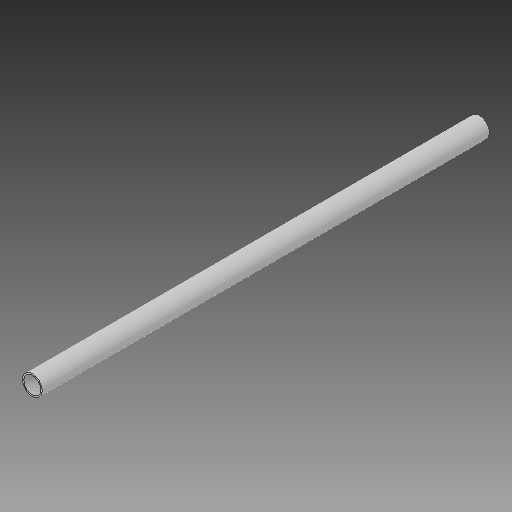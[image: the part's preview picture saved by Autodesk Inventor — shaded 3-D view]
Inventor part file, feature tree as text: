
AUTODESK INVENTOR PART (.ipt)
format: ipt  version: 2018.2 (Build 222227000, 227)  size: 80,896 bytes
history: native  units: mm
features: other x1, extrude x1, sketch x1
ambient origin geometry x8: Origin, YZ Plane, XZ Plane, XY Plane, X Axis, Y Axis, Z Axis, Center Point
bodies: Body1 (feature_tree)
feature tree (3):
  other  "ソリッド1"
  extrude  "押し出し1"  Depth=16.0mm
  sketch  "スケッチ1"
